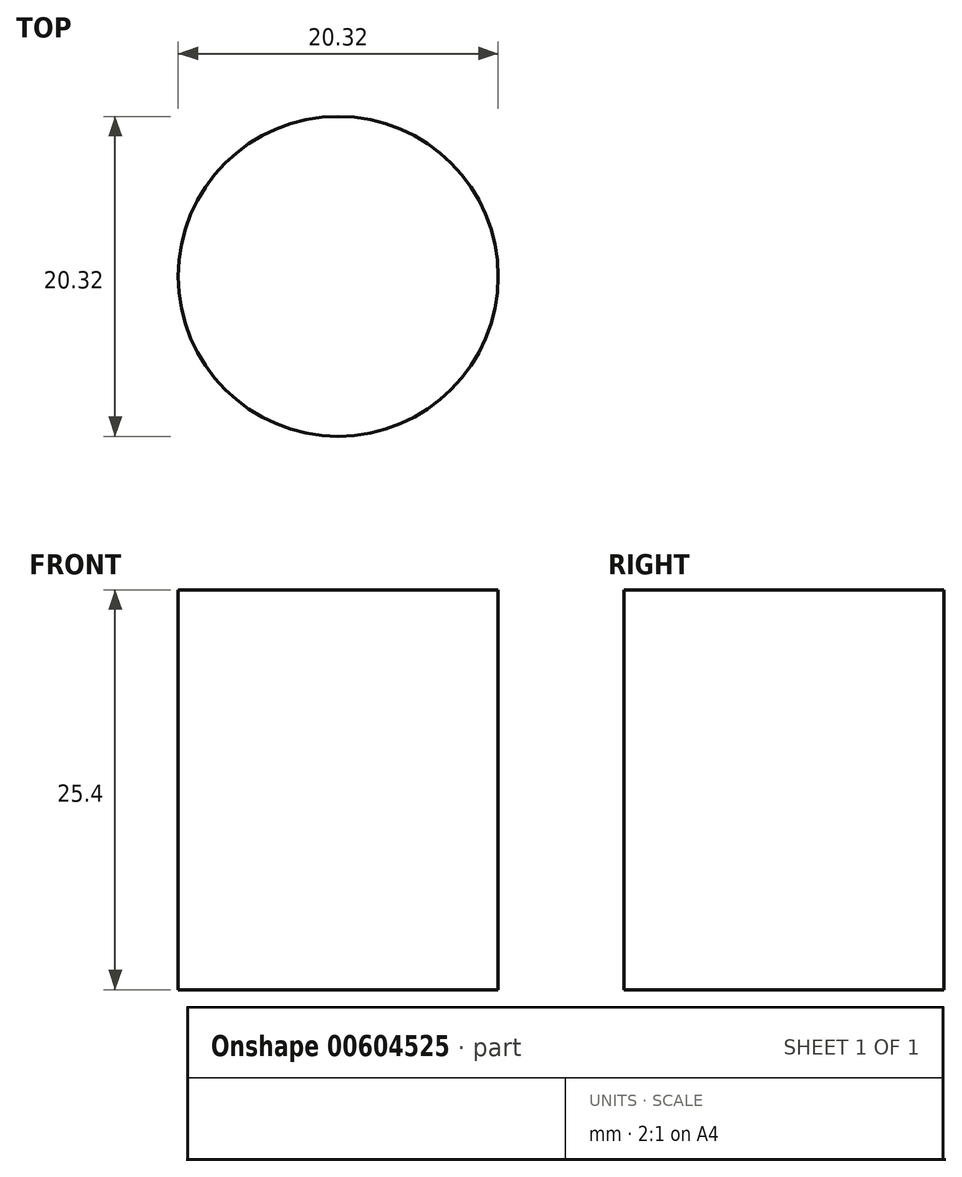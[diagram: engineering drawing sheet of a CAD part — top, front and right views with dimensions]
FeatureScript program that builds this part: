
annotation { "Feature Type Name" : "Feature", "Feature Type Description" : "" }
export const myFeature = defineFeature(function(context is Context, id is Id, definition is map)
    precondition{}
    {
        {
            var Q0;
            Q0=qCreatedBy(makeId("Top.planeOp"),FACE);
            var sketch = newSketch(context, id + "F0", { "sketchPlane" : qUnion([Q0])});
            skCircle(sketch, "E0", {"center": v(0, 0) * mm, "radius": 10.16 * mm});
            skSolve(sketch);
        }
        {
            var Q0;
            Q0 = qSketchRegion(id + "F0", true);
            var Q1;
            Q1=sQuery(id+"F0.wireOp",EDGE,"E0");
            extrude(context, id + "F1", {"entities" : qUnion([Q0]), "bodyType" : ToolBodyType.SURFACE, "surfaceEntities" : qUnion([Q1]), "depth" : 25.4 * mm, "offsetDistance" : 25.4 * mm});
        }
    });
